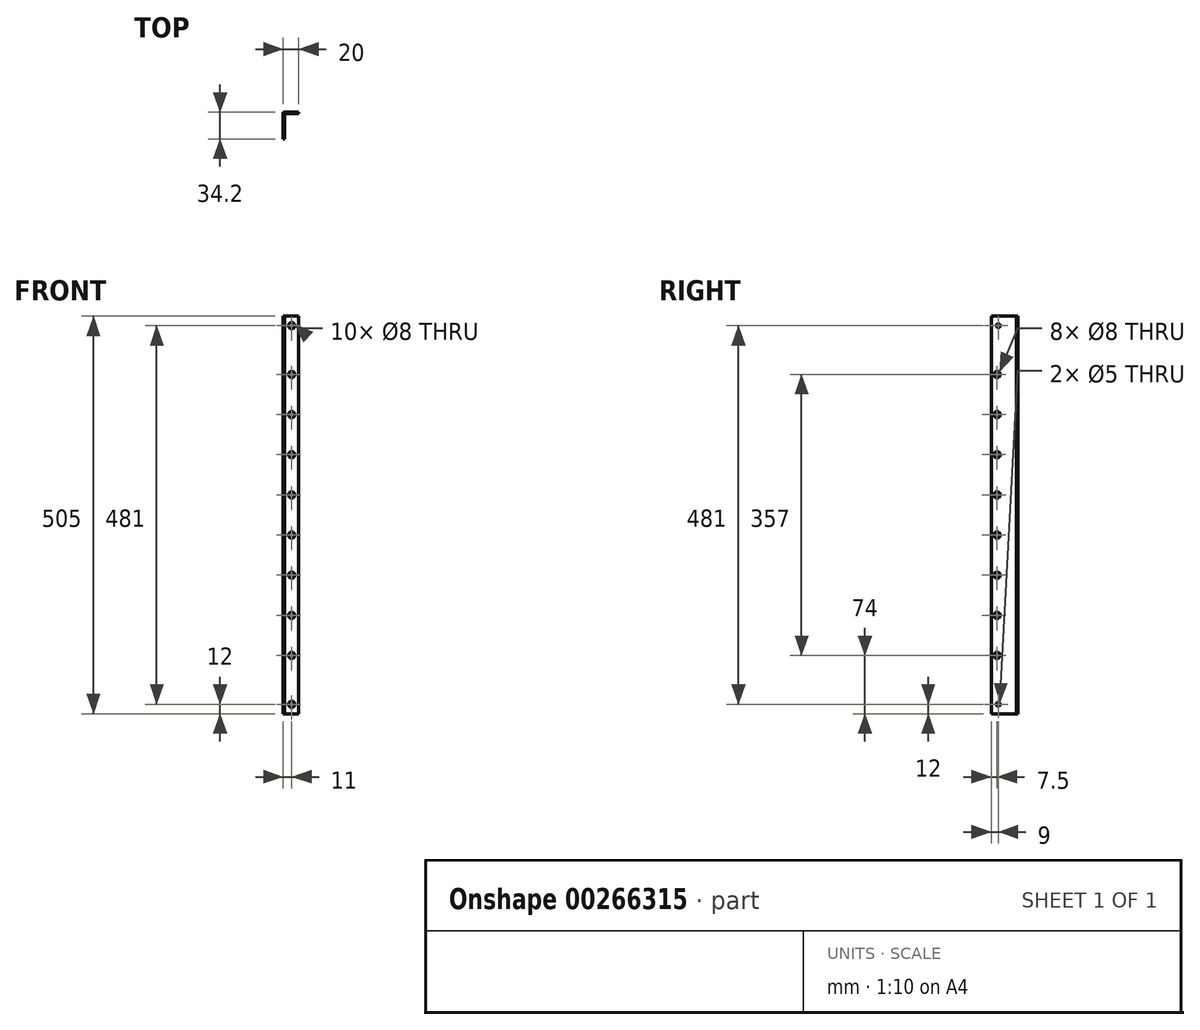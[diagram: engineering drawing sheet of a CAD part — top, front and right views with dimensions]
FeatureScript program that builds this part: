
annotation { "Feature Type Name" : "Feature", "Feature Type Description" : "" }
export const myFeature = defineFeature(function(context is Context, id is Id, definition is map)
    precondition{}
    {
        {
            var Q0;
            Q0=qCreatedBy(makeId("Top.planeOp"),FACE);
            var sketch = newSketch(context, id + "F0", { "sketchPlane" : qUnion([Q0])});
            skLineSegment(sketch, "E0", {"start": v(0, 0) * mm, "end": v(2, 0) * mm});
            skLineSegment(sketch, "E1", {"start": v(2, 0) * mm, "end": v(2, 32.2) * mm});
            skLineSegment(sketch, "E2", {"start": v(2, 32.2) * mm, "end": v(20, 32.2) * mm});
            skLineSegment(sketch, "E3", {"start": v(20, 32.2) * mm, "end": v(20, 34.2) * mm});
            skLineSegment(sketch, "E4", {"start": v(20, 34.2) * mm, "end": v(1.5, 34.2) * mm});
            skLineSegment(sketch, "E5", {"start": v(0, 32.7) * mm, "end": v(0, 0) * mm});
            skPoint(sketch, "E6.visualSharp", {"position": v(0, 34.2) * mm});
            skArc(sketch, "E6.filletArc", {"start": v(1.5, 34.2) * mm, "mid": v(0.44, 33.76) * mm, "end": v(0, 32.7) * mm});
            skSolve(sketch);
        }
        {
            var Q0;
            Q0=makeQuery(id+"F0.imprint","IMPRINT",FACE,{"disambiguationData":[TD([[makeQuery(id+"F0.imprint","IMPRINT",EDGE,{"derivedFrom":sQuery(id+"F0.wireOp",EDGE,"E0")}),1.0]])]});
            extrude(context, id + "F1", {"entities" : qUnion([Q0]), "depth" : 505 * mm});
        }
        {
            var Q0;
            Q0=makeQuery(id+"F1.opExtrude","SWEPT_FACE",FACE,{"disambiguationData":[OSD([sQuery(id+"F0.wireOp",EDGE,"E1")])]});
            var sketch = newSketch(context, id + "F2", { "sketchPlane" : qUnion([Q0])});
            skCircle(sketch, "E7", {"center": v(9, 493) * mm, "radius": 2.5 * mm});
            skCircle(sketch, "E8", {"center": v(7.5, 431) * mm, "radius": 4 * mm});
            skCircle(sketch, "E9", {"center": v(7.5, 74) * mm, "radius": 4 * mm});
            skCircle(sketch, "E10", {"center": v(9, 12) * mm, "radius": 2.5 * mm});
            skCircle(sketch, "E11.0.1.0", {"center": v(7.5, 380) * mm, "radius": 4 * mm});
            skCircle(sketch, "E11.0.2.0", {"center": v(7.5, 329) * mm, "radius": 4 * mm});
            skCircle(sketch, "E11.0.3.0", {"center": v(7.5, 278) * mm, "radius": 4 * mm});
            skCircle(sketch, "E11.0.4.0", {"center": v(7.5, 227) * mm, "radius": 4 * mm});
            skCircle(sketch, "E11.0.5.0", {"center": v(7.5, 176) * mm, "radius": 4 * mm});
            skCircle(sketch, "E11.0.6.0", {"center": v(7.5, 125) * mm, "radius": 4 * mm});
            skLineSegment(sketch, "E11.direction1", {"start": v(7.5, 431) * mm, "end": v(32.5, 431) * mm, "construction": true});
            skLineSegment(sketch, "E11.direction2", {"start": v(7.5, 431) * mm, "end": v(7.5, 380) * mm, "construction": true});
            skSolve(sketch);
        }
        {
            var Q0;
            Q0=makeQuery(id+"F2.imprint","IMPRINT",FACE,{"disambiguationData":[TD([[makeQuery(id+"F2.imprint","IMPRINT",EDGE,{"derivedFrom":sQuery(id+"F2.wireOp",EDGE,"E8")}),1.0]])]});
            var Q1;
            Q1=makeQuery(id+"F2.imprint","IMPRINT",FACE,{"disambiguationData":[TD([[makeQuery(id+"F2.imprint","IMPRINT",EDGE,{"derivedFrom":sQuery(id+"F2.wireOp",EDGE,"E11.0.1.0")}),1.0]])]});
            var Q2;
            Q2=makeQuery(id+"F2.imprint","IMPRINT",FACE,{"disambiguationData":[TD([[makeQuery(id+"F2.imprint","IMPRINT",EDGE,{"derivedFrom":sQuery(id+"F2.wireOp",EDGE,"E11.0.2.0")}),1.0]])]});
            var Q3;
            Q3=makeQuery(id+"F2.imprint","IMPRINT",FACE,{"disambiguationData":[TD([[makeQuery(id+"F2.imprint","IMPRINT",EDGE,{"derivedFrom":sQuery(id+"F2.wireOp",EDGE,"E11.0.3.0")}),1.0]])]});
            var Q4;
            Q4=makeQuery(id+"F2.imprint","IMPRINT",FACE,{"disambiguationData":[TD([[makeQuery(id+"F2.imprint","IMPRINT",EDGE,{"derivedFrom":sQuery(id+"F2.wireOp",EDGE,"E11.0.4.0")}),1.0]])]});
            var Q5;
            Q5=makeQuery(id+"F2.imprint","IMPRINT",FACE,{"disambiguationData":[TD([[makeQuery(id+"F2.imprint","IMPRINT",EDGE,{"derivedFrom":sQuery(id+"F2.wireOp",EDGE,"E11.0.5.0")}),1.0]])]});
            var Q6;
            Q6=makeQuery(id+"F2.imprint","IMPRINT",FACE,{"disambiguationData":[TD([[makeQuery(id+"F2.imprint","IMPRINT",EDGE,{"derivedFrom":sQuery(id+"F2.wireOp",EDGE,"E11.0.6.0")}),1.0]])]});
            var Q7;
            Q7=makeQuery(id+"F2.imprint","IMPRINT",FACE,{"disambiguationData":[TD([[makeQuery(id+"F2.imprint","IMPRINT",EDGE,{"derivedFrom":sQuery(id+"F2.wireOp",EDGE,"E9")}),1.0]])]});
            var Q8;
            Q8=makeQuery(id+"F2.imprint","IMPRINT",FACE,{"disambiguationData":[TD([[makeQuery(id+"F2.imprint","IMPRINT",EDGE,{"derivedFrom":sQuery(id+"F2.wireOp",EDGE,"E10")}),1.0]])]});
            var Q9;
            Q9=makeQuery(id+"F2.imprint","IMPRINT",FACE,{"disambiguationData":[TD([[makeQuery(id+"F2.imprint","IMPRINT",EDGE,{"derivedFrom":sQuery(id+"F2.wireOp",EDGE,"E7")}),1.0]])]});
            var Q10;
            Q10=sQuery(id+"F2.wireOp",EDGE,"JpF69OEy-0Npn-QOIM-1hPU-cjhVNGXRYLCI");
            var Q11;
            Q11=sQuery(id+"F2.wireOp",EDGE,"E8");
            var Q12;
            Q12=sQuery(id+"F2.wireOp",EDGE,"E7");
            var Q13;
            Q13=sQuery(id+"F2.wireOp",EDGE,"dda5dc4a-59b0-4335-ac76-f47cb5181846.0.1.0");
            var Q14;
            Q14=sQuery(id+"F2.wireOp",EDGE,"dda5dc4a-59b0-4335-ac76-f47cb5181846.0.2.0");
            var Q15;
            Q15=sQuery(id+"F2.wireOp",EDGE,"dda5dc4a-59b0-4335-ac76-f47cb5181846.0.3.0");
            var Q16;
            Q16=sQuery(id+"F2.wireOp",EDGE,"dda5dc4a-59b0-4335-ac76-f47cb5181846.0.4.0");
            var Q17;
            Q17=sQuery(id+"F2.wireOp",EDGE,"dda5dc4a-59b0-4335-ac76-f47cb5181846.0.5.0");
            var Q18;
            Q18=sQuery(id+"F2.wireOp",EDGE,"E9");
            var Q19;
            Q19=sQuery(id+"F2.wireOp",EDGE,"E10");
            extrude(context, id + "F3", {"entities" : qUnion([Q0, Q1, Q2, Q3, Q4, Q5, Q6, Q7, Q8, Q9]), "operationType" : NewBodyOperationType.REMOVE, "surfaceEntities" : qUnion([Q10, Q11, Q12, Q13, Q14, Q15, Q16, Q17, Q18, Q19]), "endBound" : BoundingType.THROUGH_ALL, "oppositeDirection" : true, "depth" : 25 * mm});
        }
        {
            var Q0;
            Q0=makeQuery(id+"F1.opExtrude","SWEPT_FACE",FACE,{"disambiguationData":[OSD([sQuery(id+"F0.wireOp",EDGE,"E2")])]});
            var sketch = newSketch(context, id + "F4", { "sketchPlane" : qUnion([Q0])});
            skCircle(sketch, "E12", {"center": v(11, 493) * mm, "radius": 4 * mm});
            skPoint(sketch, "E12.centerSnap0", {"position": v(11, 505) * mm});
            skCircle(sketch, "E13", {"center": v(11, 431) * mm, "radius": 4 * mm});
            skCircle(sketch, "E14.0.1.0", {"center": v(11, 380) * mm, "radius": 4 * mm});
            skCircle(sketch, "E14.0.2.0", {"center": v(11, 329) * mm, "radius": 4 * mm});
            skCircle(sketch, "E14.0.3.0", {"center": v(11, 278) * mm, "radius": 4 * mm});
            skCircle(sketch, "E14.0.4.0", {"center": v(11, 227) * mm, "radius": 4 * mm});
            skCircle(sketch, "E14.0.5.0", {"center": v(11, 176) * mm, "radius": 4 * mm});
            skCircle(sketch, "E14.0.6.0", {"center": v(11, 125) * mm, "radius": 4 * mm});
            skLineSegment(sketch, "E14.direction1", {"start": v(11, 431) * mm, "end": v(62, 431) * mm, "construction": true});
            skLineSegment(sketch, "E14.direction2", {"start": v(11, 431) * mm, "end": v(11, 380) * mm, "construction": true});
            skCircle(sketch, "E15.0.1.0", {"center": v(11, 12) * mm, "radius": 4 * mm});
            skLineSegment(sketch, "E15.direction1", {"start": v(11, 493) * mm, "end": v(36, 493) * mm, "construction": true});
            skLineSegment(sketch, "E15.direction2", {"start": v(11, 493) * mm, "end": v(11, 12) * mm, "construction": true});
            skCircle(sketch, "E16.0.0.7", {"center": v(11, 74) * mm, "radius": 4 * mm});
            skSolve(sketch);
        }
        {
            var Q0;
            Q0=makeQuery(id+"F4.imprint","IMPRINT",FACE,{"disambiguationData":[TD([[makeQuery(id+"F4.imprint","IMPRINT",EDGE,{"derivedFrom":sQuery(id+"F4.wireOp",EDGE,"E16.0.0.7")}),1.0]])]});
            var Q1;
            Q1=makeQuery(id+"F4.imprint","IMPRINT",FACE,{"disambiguationData":[TD([[makeQuery(id+"F4.imprint","IMPRINT",EDGE,{"derivedFrom":sQuery(id+"F4.wireOp",EDGE,"E14.0.6.0")}),1.0]])]});
            var Q2;
            Q2=makeQuery(id+"F4.imprint","IMPRINT",FACE,{"disambiguationData":[TD([[makeQuery(id+"F4.imprint","IMPRINT",EDGE,{"derivedFrom":sQuery(id+"F4.wireOp",EDGE,"E15.0.1.0")}),1.0]])]});
            var Q3;
            Q3=makeQuery(id+"F4.imprint","IMPRINT",FACE,{"disambiguationData":[TD([[makeQuery(id+"F4.imprint","IMPRINT",EDGE,{"derivedFrom":sQuery(id+"F4.wireOp",EDGE,"E14.0.5.0")}),1.0]])]});
            var Q4;
            Q4=makeQuery(id+"F4.imprint","IMPRINT",FACE,{"disambiguationData":[TD([[makeQuery(id+"F4.imprint","IMPRINT",EDGE,{"derivedFrom":sQuery(id+"F4.wireOp",EDGE,"E14.0.4.0")}),1.0]])]});
            var Q5;
            Q5=makeQuery(id+"F4.imprint","IMPRINT",FACE,{"disambiguationData":[TD([[makeQuery(id+"F4.imprint","IMPRINT",EDGE,{"derivedFrom":sQuery(id+"F4.wireOp",EDGE,"E14.0.3.0")}),1.0]])]});
            var Q6;
            Q6=makeQuery(id+"F4.imprint","IMPRINT",FACE,{"disambiguationData":[TD([[makeQuery(id+"F4.imprint","IMPRINT",EDGE,{"derivedFrom":sQuery(id+"F4.wireOp",EDGE,"E14.0.2.0")}),1.0]])]});
            var Q7;
            Q7=makeQuery(id+"F4.imprint","IMPRINT",FACE,{"disambiguationData":[TD([[makeQuery(id+"F4.imprint","IMPRINT",EDGE,{"derivedFrom":sQuery(id+"F4.wireOp",EDGE,"E14.0.1.0")}),1.0]])]});
            var Q8;
            Q8=makeQuery(id+"F4.imprint","IMPRINT",FACE,{"disambiguationData":[TD([[makeQuery(id+"F4.imprint","IMPRINT",EDGE,{"derivedFrom":sQuery(id+"F4.wireOp",EDGE,"E13")}),1.0]])]});
            var Q9;
            Q9=makeQuery(id+"F4.imprint","IMPRINT",FACE,{"disambiguationData":[TD([[makeQuery(id+"F4.imprint","IMPRINT",EDGE,{"derivedFrom":sQuery(id+"F4.wireOp",EDGE,"E12")}),1.0]])]});
            var Q10;
            Q10=sQuery(id+"F4.wireOp",EDGE,"E12");
            var Q11;
            Q11=sQuery(id+"F4.wireOp",EDGE,"E13");
            var Q12;
            Q12=sQuery(id+"F4.wireOp",EDGE,"E14.0.1.0");
            var Q13;
            Q13=sQuery(id+"F4.wireOp",EDGE,"E14.0.2.0");
            var Q14;
            Q14=sQuery(id+"F4.wireOp",EDGE,"E14.0.3.0");
            var Q15;
            Q15=sQuery(id+"F4.wireOp",EDGE,"E14.0.4.0");
            var Q16;
            Q16=sQuery(id+"F4.wireOp",EDGE,"E14.0.5.0");
            var Q17;
            Q17=sQuery(id+"F4.wireOp",EDGE,"E14.0.6.0");
            var Q18;
            Q18=sQuery(id+"F4.wireOp",EDGE,"E14.0.7.0");
            var Q19;
            Q19=sQuery(id+"F4.wireOp",EDGE,"E15.0.1.0");
            extrude(context, id + "F5", {"entities" : qUnion([Q0, Q1, Q2, Q3, Q4, Q5, Q6, Q7, Q8, Q9]), "operationType" : NewBodyOperationType.REMOVE, "surfaceEntities" : qUnion([Q10, Q11, Q12, Q13, Q14, Q15, Q16, Q17, Q18, Q19]), "endBound" : BoundingType.THROUGH_ALL, "oppositeDirection" : true, "depth" : 25 * mm});
        }
    });
